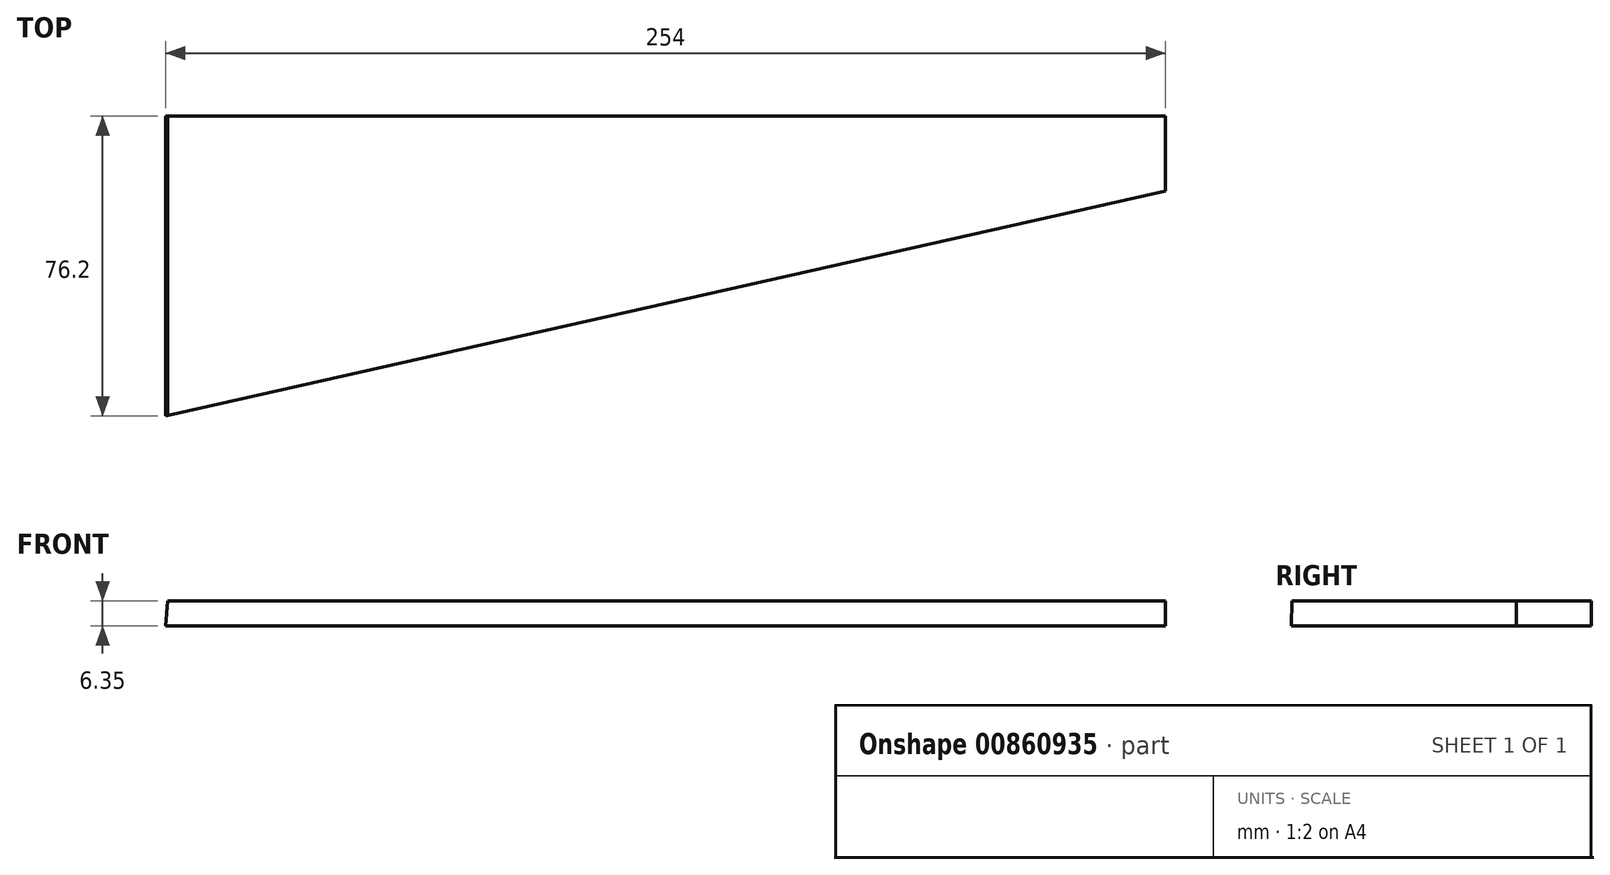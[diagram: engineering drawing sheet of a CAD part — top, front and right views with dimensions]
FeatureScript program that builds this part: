
annotation { "Feature Type Name" : "Feature", "Feature Type Description" : "" }
export const myFeature = defineFeature(function(context is Context, id is Id, definition is map)
    precondition{}
    {
        {
            var Q0;
            Q0=qCreatedBy(makeId("Top.planeOp"),FACE);
            var sketch = newSketch(context, id + "F0", { "sketchPlane" : qUnion([Q0])});
            skLineSegment(sketch, "E0.bottom", {"start": v(-126.07, 38.81) * mm, "end": v(127.93, 38.81) * mm});
            skLineSegment(sketch, "E0.left", {"start": v(-126.07, 38.81) * mm, "end": v(-126.07, -37.39) * mm});
            skLineSegment(sketch, "E0.right", {"start": v(127.93, 38.81) * mm, "end": v(127.93, 19.76) * mm});
            skLineSegment(sketch, "E1", {"start": v(-126.07, -37.39) * mm, "end": v(127.93, 19.76) * mm});
            skSolve(sketch);
        }
        {
            var Q0;
            Q0=makeQuery(id+"F0.imprint","IMPRINT",FACE,{"disambiguationData":[TD([[makeQuery(id+"F0.imprint","IMPRINT",EDGE,{"derivedFrom":sQuery(id+"F0.wireOp",EDGE,"E0.bottom")}),-1.0]])]});
            extrude(context, id + "F1", {"entities" : qUnion([Q0]), "depth" : 6.35 * mm, "offsetDistance" : 25.4 * mm});
        }
        {
            var Q0;
            Q0=makeQuery(id+"F1.opExtrude","SWEPT_FACE",FACE,{"disambiguationData":[OSD([sQuery(id+"F0.wireOp",EDGE,"E0.bottom")])]});
            var sketch = newSketch(context, id + "F2", { "sketchPlane" : qUnion([Q0])});
            skLineSegment(sketch, "E2", {"start": v(126.07, 0) * mm, "end": v(125.56, 6.35) * mm});
            skLineSegment(sketch, "E3", {"start": v(125.56, 6.35) * mm, "end": v(126.07, 6.35) * mm});
            skLineSegment(sketch, "E4", {"start": v(126.07, 6.35) * mm, "end": v(126.07, 0) * mm});
            skSolve(sketch);
        }
        {
            var Q0;
            Q0=makeQuery(id+"F2.imprint","IMPRINT",FACE,{"disambiguationData":[TD([[makeQuery(id+"F2.imprint","IMPRINT",EDGE,{"derivedFrom":sQuery(id+"F2.wireOp",EDGE,"E2")}),-1.0]])]});
            extrude(context, id + "F3", {"entities" : qUnion([Q0]), "operationType" : NewBodyOperationType.REMOVE, "oppositeDirection" : true, "depth" : 86.61 * mm, "offsetDistance" : 25.4 * mm});
        }
    });
